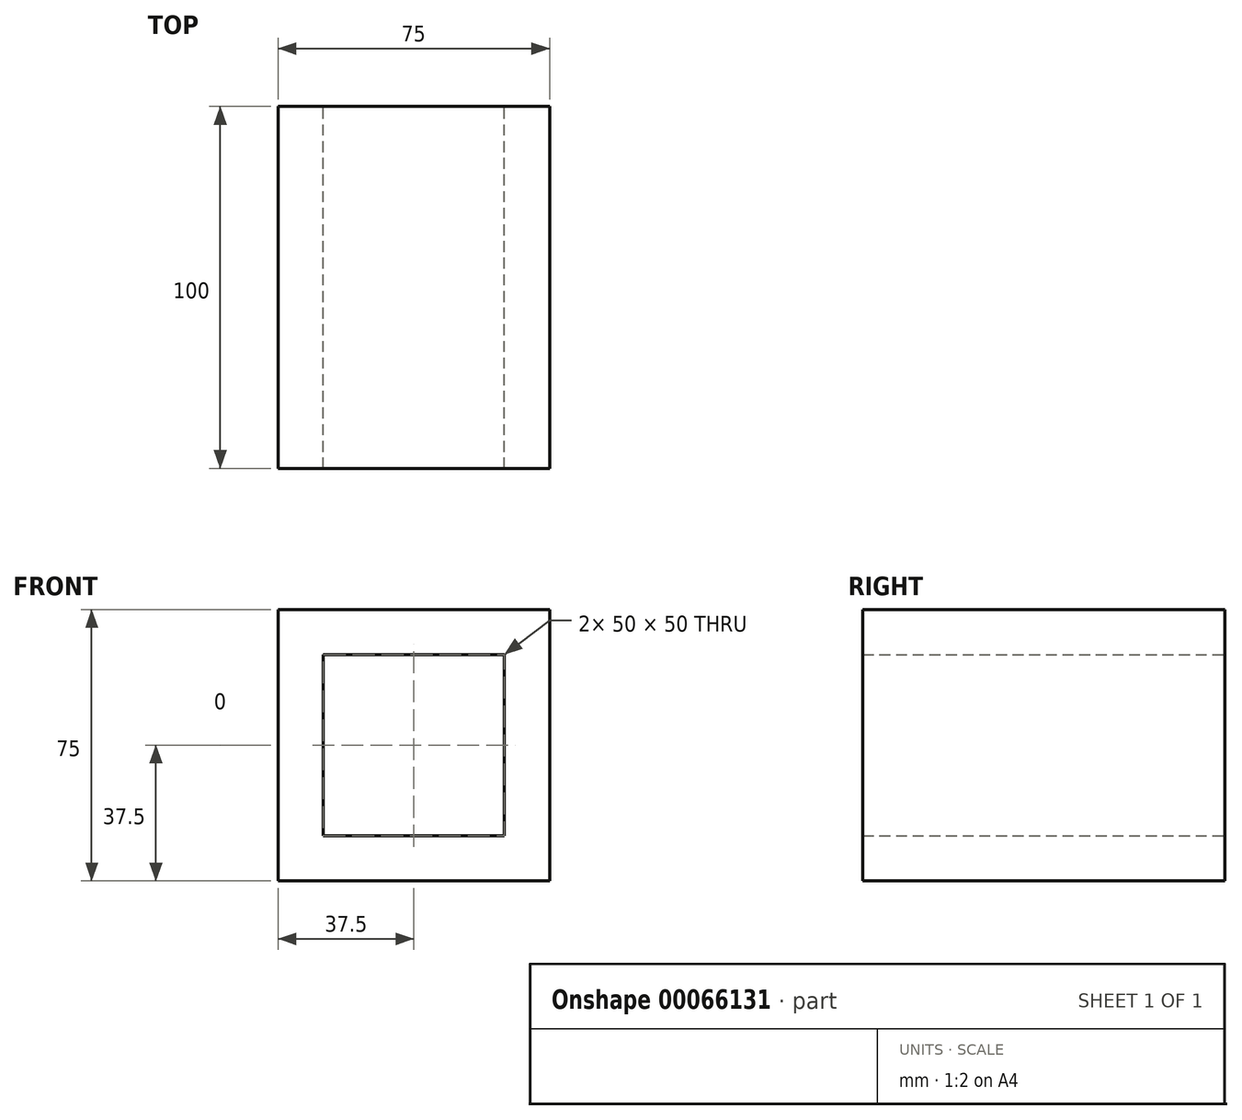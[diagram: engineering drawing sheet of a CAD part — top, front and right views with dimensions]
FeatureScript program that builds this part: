
annotation { "Feature Type Name" : "Feature", "Feature Type Description" : "" }
export const myFeature = defineFeature(function(context is Context, id is Id, definition is map)
    precondition{}
    {
        {
            var Q0;
            Q0=qCreatedBy(makeId("Front.planeOp"),FACE);
            var sketch = newSketch(context, id + "F0", { "sketchPlane" : qUnion([Q0])});
            skLineSegment(sketch, "E0.rect.bottom", {"start": v(-25, 25) * mm, "end": v(25, 25) * mm});
            skLineSegment(sketch, "E0.rect.top", {"start": v(-25, -25) * mm, "end": v(25, -25) * mm});
            skLineSegment(sketch, "E0.rect.left", {"start": v(-25, 25) * mm, "end": v(-25, -25) * mm});
            skLineSegment(sketch, "E0.rect.right", {"start": v(25, 25) * mm, "end": v(25, -25) * mm});
            skPoint(sketch, "E0.rect.middle", {"position": v(0, 0) * mm});
            skLineSegment(sketch, "E1.rect.bottom", {"start": v(-37.5, 37.5) * mm, "end": v(37.5, 37.5) * mm});
            skLineSegment(sketch, "E1.rect.top", {"start": v(-37.5, -37.5) * mm, "end": v(37.5, -37.5) * mm});
            skLineSegment(sketch, "E1.rect.left", {"start": v(-37.5, 37.5) * mm, "end": v(-37.5, -37.5) * mm});
            skLineSegment(sketch, "E1.rect.right", {"start": v(37.5, 37.5) * mm, "end": v(37.5, -37.5) * mm});
            skSolve(sketch);
        }
        {
            var Q0;
            Q0 = qSketchRegion(id + "F0", true);
            extrude(context, id + "F1", {"entities" : qUnion([Q0]), "depth" : 100 * mm});
        }
    });
